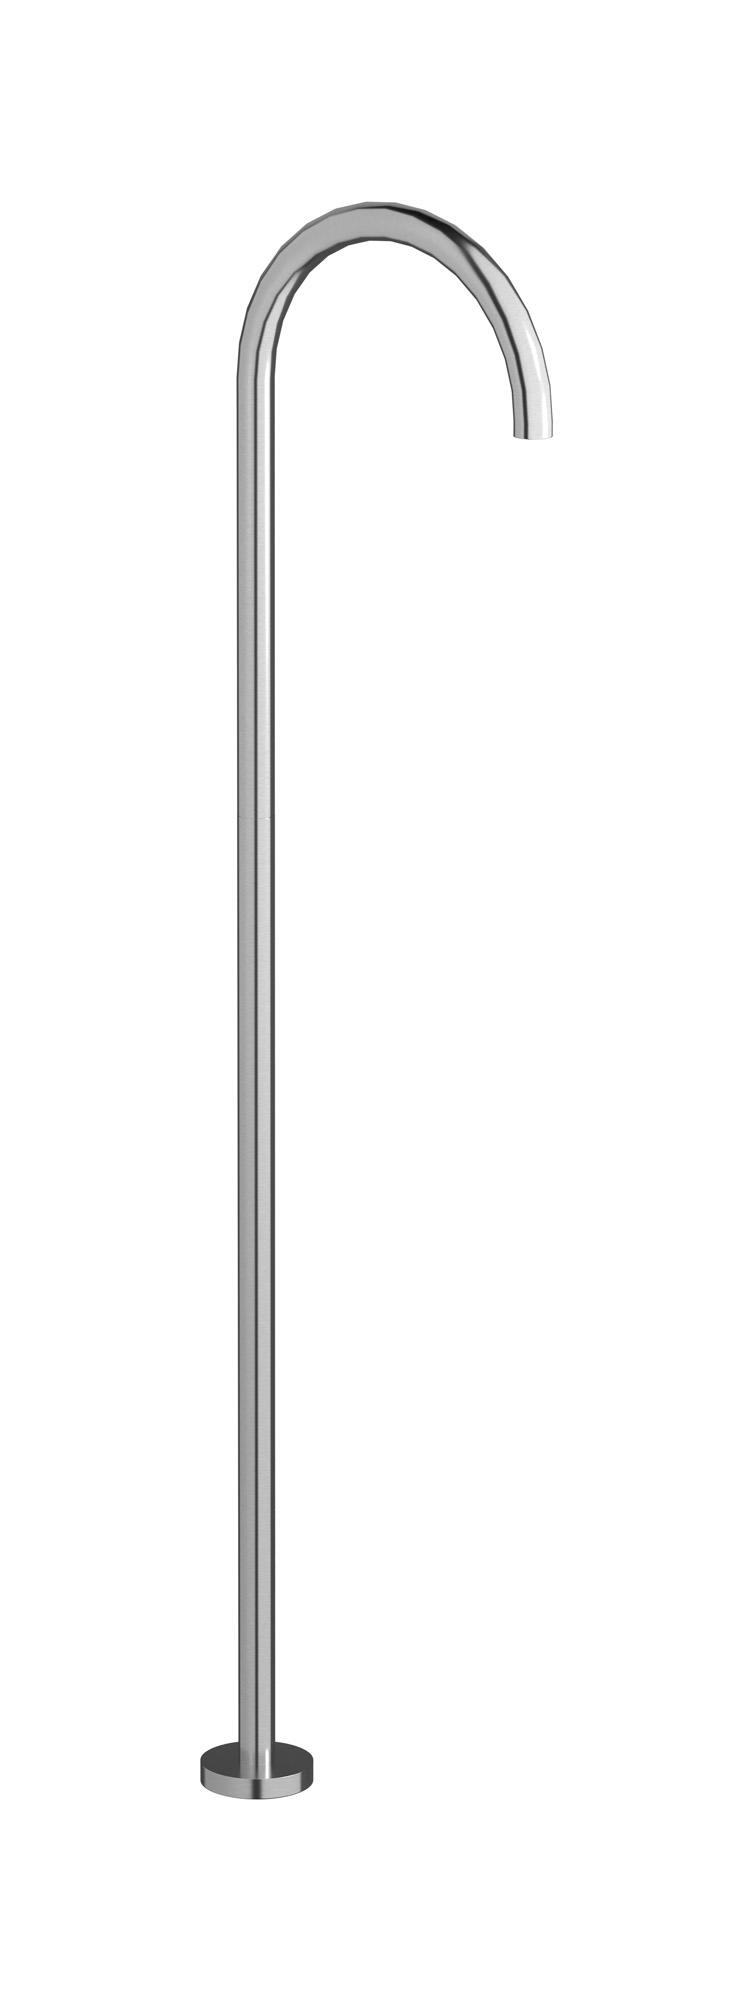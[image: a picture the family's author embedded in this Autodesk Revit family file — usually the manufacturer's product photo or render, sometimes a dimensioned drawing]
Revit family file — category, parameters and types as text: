
# Revit family: RX299
name_source: partatom
category: Apparecchi idraulici
units: mm (PartAtom-declared; Revit-internal decimal feet)

## family parameters
Basato su piano di lavoro = No
Condiviso = No
Mantieni orientamento annotazione = No
Numero OmniClass = 23.45.55.17
Punto di calcolo locali = No
Quota connettore circolare = Usa diametro
Sempre verticale = Sì
Taglio con vuoti quando caricato = No
Tipo di parte = Normale
Titolo OmniClass = Mixing Faucets

## types (12) — shared parameters
Commenti sul tipo = Free standing washbasin spout complete with drain
Connessione CW = No
Connessione HW = No
Connessione di scarico = No
Connessione di ventilazione = No
Descrizione = Free standing washbasin spout complete with drain
Produttore = IB Rubinetterie S.p.A.
URL = https://www.weareib.it
Water inlet = 10 mm  [stored 0.0328084 ft]
zero-valued in all types: Prospetto di default

## per-type parameters (varying)
| type | Finishes surface | Immagine tipo | Modello |
| Chrome | IB_Chrome | RX299CC.jpg | RX299CC |
| Black Chrome | IB_Black chrome | RX299CF.jpg | RX299CF |
| Brushed Black Chrome | IB_Brushed black chrome | RX299CS.jpg | RX299CS |
| Pale Gold | IB_Pale gold | RX299II.jpg | RX299II |
| Brushed Pale Gold | IB_brushed pale gold | RX299IS.jpg | RX299IS |
| Matt Black | IB_matt black | RX299NP.jpg | RX299NP |
| Natural Brass | IB_Brass | RX299ON.jpg | RX299ON |
| Gold | IB_gold | RX299OO.jpg | RX299OO |
| Brushed Gold | IB_brushed gold | RX299OS.jpg | RX299OS |
| Rose Gold | IB_Rose gold | RX299RS.jpg | RX299RS |
| Brushed Rose Gold | IB_Brushed rose gold | RX299SR.jpg | RX299SR |
| Brushed Nickel | IB_Brushed nickel | RX299SS.jpg | RX299SS |

note: [stored X ft] marks values corroborated as IEEE doubles in the binary element streams (Revit-internal decimal feet)
